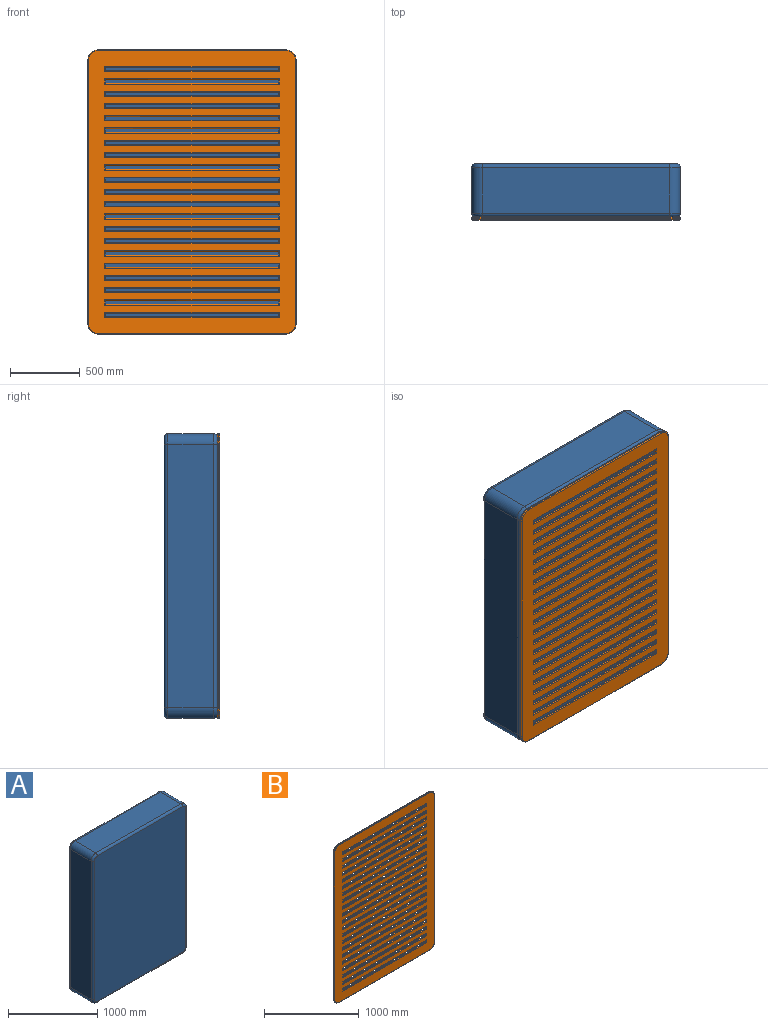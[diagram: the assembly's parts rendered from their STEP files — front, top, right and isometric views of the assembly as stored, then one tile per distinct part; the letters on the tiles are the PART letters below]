
ASSEMBLY  parts=2 mates=1
PART A: 26 faces, bbox 1511.2x381x2057.3 mm
  f0: plane 1892.3x330.2mm, normal (-1,0,0), area 624837.5mm2, adj f1,f7,f14,f22
  f1: cylinder r=76.2mm len=330.2mm, axis (0,1,0), area 39523.2mm2, adj f0,f2,f12,f20
  f2: plane 1346.2x330.2mm, normal (0,0,-1), area 444515.2mm2, adj f1,f3,f10,f18
  f3: cylinder r=76.2mm len=330.2mm, axis (0,1,0), area 39523.2mm2, adj f2,f4,f11,f19
  f4: plane 1892.3x330.2mm, normal (1,0,0), area 624837.5mm2, adj f3,f5,f13,f21
  f5: cylinder r=76.2mm len=330.2mm, axis (0,1,0), area 39523.2mm2, adj f4,f6,f15,f23
  f6: plane 1346.2x330.2mm, normal (0,0,1), area 444515.2mm2, adj f5,f7,f17,f25
  f7: cylinder r=76.2mm len=330.2mm, axis (0,1,0), area 39523.2mm2, adj f0,f6,f16,f24
  f8: plane 1993.9x1447.8mm, normal (0,-1,0), area 2884553.2mm2, adj f18,f19,f20,f21,f22,f23,f24,f25
  f9: plane 1993.9x1447.8mm, normal (0,1,0), area 2884553.2mm2, adj f10,f11,f12,f13,f14,f15,f16,f17
  f10: cylinder r=25.4mm len=1346.2mm, axis (1,0,0), area 53711mm2, adj f2,f9,f11,f12
  f11: torus R=50.8mm, axis (0,-1,0), area 4197.2mm2, adj f3,f9,f10,f13
  f12: torus R=50.8mm, axis (0,-1,0), area 4197.2mm2, adj f1,f9,f10,f14
  f13: cylinder r=25.4mm len=1892.3mm, axis (0,0,1), area 75499.4mm2, adj f4,f9,f11,f15
  f14: cylinder r=25.4mm len=1892.3mm, axis (0,0,-1), area 75499.4mm2, adj f0,f9,f12,f16
  f15: torus R=50.8mm, axis (0,-1,0), area 4197.2mm2, adj f5,f9,f13,f17
  f16: torus R=50.8mm, axis (0,-1,0), area 4197.2mm2, adj f7,f9,f14,f17
  f17: cylinder r=25.4mm len=1346.2mm, axis (-1,0,0), area 53711mm2, adj f6,f9,f15,f16
  f18: cylinder r=25.4mm len=1346.2mm, axis (-1,0,0), area 53711mm2, adj f2,f8,f19,f20
  f19: torus R=50.8mm, axis (0,-1,0), area 4197.2mm2, adj f3,f8,f18,f21
  f20: torus R=50.8mm, axis (0,-1,0), area 4197.2mm2, adj f1,f8,f18,f22
  f21: cylinder r=25.4mm len=1892.3mm, axis (0,0,-1), area 75499.4mm2, adj f4,f8,f19,f23
  f22: cylinder r=25.4mm len=1892.3mm, axis (0,0,1), area 75499.4mm2, adj f0,f8,f20,f24
  f23: torus R=50.8mm, axis (0,-1,0), area 4197.2mm2, adj f5,f8,f21,f25
  f24: torus R=50.8mm, axis (0,-1,0), area 4197.2mm2, adj f7,f8,f22,f25
  f25: cylinder r=25.4mm len=1346.2mm, axis (1,0,0), area 53711mm2, adj f6,f8,f23,f24
PART B: 278 faces, bbox 1511.2x19.1x2057.3 mm
  f0: plane 2032x1485.9mm, normal (0,-1,0), area 2009194.9mm2, adj f178,f179,f180,f181,f182,f183,f184,f185
  f1: plane 2032x1485.9mm, normal (0,1,0), area 2009194.9mm2, adj f94,f95,f96,f97,f98,f99,f100,f101
  f2: plane 1892.3x6.35mm, normal (-1,0,0), area 12016.1mm2, adj f3,f9,f266,f274
  f3: cylinder r=76.2mm len=76.2mm, axis (0,1,0), area 760.1mm2, adj f2,f4,f264,f272
  f4: plane 1346.2x6.35mm, normal (0,0,-1), area 8548.4mm2, adj f3,f5,f262,f270
  f5: cylinder r=76.2mm len=76.2mm, axis (0,1,0), area 760.1mm2, adj f4,f6,f263,f271
  f6: plane 1892.3x6.35mm, normal (1,0,0), area 12016.1mm2, adj f5,f7,f265,f273
  f7: cylinder r=76.2mm len=76.2mm, axis (0,1,0), area 760.1mm2, adj f6,f8,f267,f275
  f8: plane 1346.2x6.35mm, normal (0,0,1), area 8548.4mm2, adj f7,f9,f269,f277
  f9: cylinder r=76.2mm len=76.2mm, axis (0,1,0), area 760.1mm2, adj f2,f8,f268,f276
  f10: plane 1244.6x6.35mm, normal (0,0,-1), area 7903.2mm2, adj f11,f13,f177,f179
  f11: plane 25.4x6.35mm, normal (1,0,0), area 161.3mm2, adj f10,f12,f175,f181
  f12: plane 1244.6x6.35mm, normal (0,0,1), area 7903.2mm2, adj f11,f13,f174,f180
  f13: plane 25.4x6.35mm, normal (-1,0,0), area 161.3mm2, adj f10,f12,f176,f178
  f14: plane 1244.6x6.35mm, normal (0,0,-1), area 7903.2mm2, adj f15,f17,f173,f183
  f15: plane 25.4x6.35mm, normal (1,0,0), area 161.3mm2, adj f14,f16,f171,f185
  f16: plane 1244.6x6.35mm, normal (0,0,1), area 7903.2mm2, adj f15,f17,f170,f184
  f17: plane 25.4x6.35mm, normal (-1,0,0), area 161.3mm2, adj f14,f16,f172,f182
  f18: plane 1244.6x6.35mm, normal (0,0,-1), area 7903.2mm2, adj f19,f21,f169,f187
  f19: plane 25.4x6.35mm, normal (1,0,0), area 161.3mm2, adj f18,f20,f167,f189
  f20: plane 1244.6x6.35mm, normal (0,0,1), area 7903.2mm2, adj f19,f21,f166,f188
  f21: plane 25.4x6.35mm, normal (-1,0,0), area 161.3mm2, adj f18,f20,f168,f186
  f22: plane 1244.6x6.35mm, normal (0,0,-1), area 7903.2mm2, adj f23,f25,f165,f191
  f23: plane 25.4x6.35mm, normal (1,0,0), area 161.3mm2, adj f22,f24,f163,f193
  f24: plane 1244.6x6.35mm, normal (0,0,1), area 7903.2mm2, adj f23,f25,f162,f192
  f25: plane 25.4x6.35mm, normal (-1,0,0), area 161.3mm2, adj f22,f24,f164,f190
  f26: plane 1244.6x6.35mm, normal (0,0,-1), area 7903.2mm2, adj f27,f29,f161,f195
  f27: plane 25.4x6.35mm, normal (1,0,0), area 161.3mm2, adj f26,f28,f159,f197
  f28: plane 1244.6x6.35mm, normal (0,0,1), area 7903.2mm2, adj f27,f29,f158,f196
  f29: plane 25.4x6.35mm, normal (-1,0,0), area 161.3mm2, adj f26,f28,f160,f194
  f30: plane 1244.6x6.35mm, normal (0,0,-1), area 7903.2mm2, adj f31,f33,f157,f199
  f31: plane 25.4x6.35mm, normal (1,0,0), area 161.3mm2, adj f30,f32,f155,f201
  f32: plane 1244.6x6.35mm, normal (0,0,1), area 7903.2mm2, adj f31,f33,f154,f200
  f33: plane 25.4x6.35mm, normal (-1,0,0), area 161.3mm2, adj f30,f32,f156,f198
  f34: plane 1244.6x6.35mm, normal (0,0,-1), area 7903.2mm2, adj f35,f37,f153,f203
  f35: plane 25.4x6.35mm, normal (1,0,0), area 161.3mm2, adj f34,f36,f151,f205
  f36: plane 1244.6x6.35mm, normal (0,0,1), area 7903.2mm2, adj f35,f37,f150,f204
  f37: plane 25.4x6.35mm, normal (-1,0,0), area 161.3mm2, adj f34,f36,f152,f202
  f38: plane 1244.6x6.35mm, normal (0,0,-1), area 7903.2mm2, adj f39,f41,f149,f207
  f39: plane 25.4x6.35mm, normal (1,0,0), area 161.3mm2, adj f38,f40,f147,f209
  f40: plane 1244.6x6.35mm, normal (0,0,1), area 7903.2mm2, adj f39,f41,f146,f208
  f41: plane 25.4x6.35mm, normal (-1,0,0), area 161.3mm2, adj f38,f40,f148,f206
  f42: plane 1244.6x6.35mm, normal (0,0,-1), area 7903.2mm2, adj f43,f45,f145,f211
  f43: plane 25.4x6.35mm, normal (1,0,0), area 161.3mm2, adj f42,f44,f143,f213
  f44: plane 1244.6x6.35mm, normal (0,0,1), area 7903.2mm2, adj f43,f45,f142,f212
  f45: plane 25.4x6.35mm, normal (-1,0,0), area 161.3mm2, adj f42,f44,f144,f210
  f46: plane 1244.6x6.35mm, normal (0,0,-1), area 7903.2mm2, adj f47,f49,f141,f215
  f47: plane 25.4x6.35mm, normal (1,0,0), area 161.3mm2, adj f46,f48,f139,f217
  f48: plane 1244.6x6.35mm, normal (0,0,1), area 7903.2mm2, adj f47,f49,f138,f216
  f49: plane 25.4x6.35mm, normal (-1,0,0), area 161.3mm2, adj f46,f48,f140,f214
  f50: plane 1244.6x6.35mm, normal (0,0,-1), area 7903.2mm2, adj f51,f53,f137,f219
  f51: plane 25.4x6.35mm, normal (1,0,0), area 161.3mm2, adj f50,f52,f135,f221
  f52: plane 1244.6x6.35mm, normal (0,0,1), area 7903.2mm2, adj f51,f53,f134,f220
  f53: plane 25.4x6.35mm, normal (-1,0,0), area 161.3mm2, adj f50,f52,f136,f218
  f54: plane 1244.6x6.35mm, normal (0,0,-1), area 7903.2mm2, adj f55,f57,f133,f223
  f55: plane 25.4x6.35mm, normal (1,0,0), area 161.3mm2, adj f54,f56,f131,f225
  f56: plane 1244.6x6.35mm, normal (0,0,1), area 7903.2mm2, adj f55,f57,f130,f224
  f57: plane 25.4x6.35mm, normal (-1,0,0), area 161.3mm2, adj f54,f56,f132,f222
  f58: plane 1244.6x6.35mm, normal (0,0,-1), area 7903.2mm2, adj f59,f61,f129,f227
  f59: plane 25.4x6.35mm, normal (1,0,0), area 161.3mm2, adj f58,f60,f127,f229
  f60: plane 1244.6x6.35mm, normal (0,0,1), area 7903.2mm2, adj f59,f61,f126,f228
  f61: plane 25.4x6.35mm, normal (-1,0,0), area 161.3mm2, adj f58,f60,f128,f226
  f62: plane 1244.6x6.35mm, normal (0,0,-1), area 7903.2mm2, adj f63,f65,f125,f231
  f63: plane 25.4x6.35mm, normal (1,0,0), area 161.3mm2, adj f62,f64,f123,f233
  f64: plane 1244.6x6.35mm, normal (0,0,1), area 7903.2mm2, adj f63,f65,f122,f232
  f65: plane 25.4x6.35mm, normal (-1,0,0), area 161.3mm2, adj f62,f64,f124,f230
  f66: plane 1244.6x6.35mm, normal (0,0,-1), area 7903.2mm2, adj f67,f69,f121,f235
  f67: plane 25.4x6.35mm, normal (1,0,0), area 161.3mm2, adj f66,f68,f119,f237
  f68: plane 1244.6x6.35mm, normal (0,0,1), area 7903.2mm2, adj f67,f69,f118,f236
  f69: plane 25.4x6.35mm, normal (-1,0,0), area 161.3mm2, adj f66,f68,f120,f234
  f70: plane 1244.6x6.35mm, normal (0,0,-1), area 7903.2mm2, adj f71,f73,f117,f239
  f71: plane 25.4x6.35mm, normal (1,0,0), area 161.3mm2, adj f70,f72,f115,f241
  f72: plane 1244.6x6.35mm, normal (0,0,1), area 7903.2mm2, adj f71,f73,f114,f240
  f73: plane 25.4x6.35mm, normal (-1,0,0), area 161.3mm2, adj f70,f72,f116,f238
  f74: plane 1244.6x6.35mm, normal (0,0,-1), area 7903.2mm2, adj f75,f77,f113,f243
  f75: plane 25.4x6.35mm, normal (1,0,0), area 161.3mm2, adj f74,f76,f111,f245
  f76: plane 1244.6x6.35mm, normal (0,0,1), area 7903.2mm2, adj f75,f77,f110,f244
  f77: plane 25.4x6.35mm, normal (-1,0,0), area 161.3mm2, adj f74,f76,f112,f242
  f78: plane 1244.6x6.35mm, normal (0,0,-1), area 7903.2mm2, adj f79,f81,f109,f247
  f79: plane 25.4x6.35mm, normal (1,0,0), area 161.3mm2, adj f78,f80,f107,f249
  f80: plane 1244.6x6.35mm, normal (0,0,1), area 7903.2mm2, adj f79,f81,f106,f248
  f81: plane 25.4x6.35mm, normal (-1,0,0), area 161.3mm2, adj f78,f80,f108,f246
  f82: plane 1244.6x6.35mm, normal (0,0,-1), area 7903.2mm2, adj f83,f85,f105,f251
  f83: plane 25.4x6.35mm, normal (1,0,0), area 161.3mm2, adj f82,f84,f103,f253
  f84: plane 1244.6x6.35mm, normal (0,0,1), area 7903.2mm2, adj f83,f85,f102,f252
  f85: plane 25.4x6.35mm, normal (-1,0,0), area 161.3mm2, adj f82,f84,f104,f250
  f86: plane 1244.6x6.35mm, normal (0,0,-1), area 7903.2mm2, adj f87,f89,f101,f254
  f87: plane 25.4x6.35mm, normal (1,0,0), area 161.3mm2, adj f86,f88,f99,f255
  f88: plane 1244.6x6.35mm, normal (0,0,1), area 7903.2mm2, adj f87,f89,f98,f257
  f89: plane 25.4x6.35mm, normal (-1,0,0), area 161.3mm2, adj f86,f88,f100,f256
  f90: plane 1244.6x6.35mm, normal (0,0,-1), area 7903.2mm2, adj f91,f93,f97,f259
  f91: plane 25.4x6.35mm, normal (1,0,0), area 161.3mm2, adj f90,f92,f95,f261
  f92: plane 1244.6x6.35mm, normal (0,0,1), area 7903.2mm2, adj f91,f93,f94,f260
  f93: plane 25.4x6.35mm, normal (-1,0,0), area 161.3mm2, adj f90,f92,f96,f258
  f94: cylinder r=6.35mm len=1257.3mm, axis (1,0,0), area 12460.4mm2, adj f1,f92,f95,f96
  f95: cylinder r=6.35mm len=38.1mm, axis (0,0,-1), area 299.4mm2, adj f1,f91,f94,f97
  f96: cylinder r=6.35mm len=38.1mm, axis (0,0,1), area 299.4mm2, adj f1,f93,f94,f97
  f97: cylinder r=6.35mm len=1257.3mm, axis (-1,0,0), area 12460.4mm2, adj f1,f90,f95,f96
  f98: cylinder r=6.35mm len=1257.3mm, axis (1,0,0), area 12460.4mm2, adj f1,f88,f99,f100
  f99: cylinder r=6.35mm len=38.1mm, axis (0,0,-1), area 299.4mm2, adj f1,f87,f98,f101
  f100: cylinder r=6.35mm len=38.1mm, axis (0,0,1), area 299.4mm2, adj f1,f89,f98,f101
  f101: cylinder r=6.35mm len=1257.3mm, axis (-1,0,0), area 12460.4mm2, adj f1,f86,f99,f100
  f102: cylinder r=6.35mm len=1257.3mm, axis (1,0,0), area 12460.4mm2, adj f1,f84,f103,f104
  f103: cylinder r=6.35mm len=38.1mm, axis (0,0,-1), area 299.4mm2, adj f1,f83,f102,f105
  f104: cylinder r=6.35mm len=38.1mm, axis (0,0,1), area 299.4mm2, adj f1,f85,f102,f105
  f105: cylinder r=6.35mm len=1257.3mm, axis (-1,0,0), area 12460.4mm2, adj f1,f82,f103,f104
  f106: cylinder r=6.35mm len=1257.3mm, axis (1,0,0), area 12460.4mm2, adj f1,f80,f107,f108
  f107: cylinder r=6.35mm len=38.1mm, axis (0,0,-1), area 299.4mm2, adj f1,f79,f106,f109
  f108: cylinder r=6.35mm len=38.1mm, axis (0,0,1), area 299.4mm2, adj f1,f81,f106,f109
  f109: cylinder r=6.35mm len=1257.3mm, axis (-1,0,0), area 12460.4mm2, adj f1,f78,f107,f108
  f110: cylinder r=6.35mm len=1257.3mm, axis (1,0,0), area 12460.4mm2, adj f1,f76,f111,f112
  f111: cylinder r=6.35mm len=38.1mm, axis (0,0,-1), area 299.4mm2, adj f1,f75,f110,f113
  f112: cylinder r=6.35mm len=38.1mm, axis (0,0,1), area 299.4mm2, adj f1,f77,f110,f113
  f113: cylinder r=6.35mm len=1257.3mm, axis (-1,0,0), area 12460.4mm2, adj f1,f74,f111,f112
  f114: cylinder r=6.35mm len=1257.3mm, axis (1,0,0), area 12460.4mm2, adj f1,f72,f115,f116
  f115: cylinder r=6.35mm len=38.1mm, axis (0,0,-1), area 299.4mm2, adj f1,f71,f114,f117
  f116: cylinder r=6.35mm len=38.1mm, axis (0,0,1), area 299.4mm2, adj f1,f73,f114,f117
  f117: cylinder r=6.35mm len=1257.3mm, axis (-1,0,0), area 12460.4mm2, adj f1,f70,f115,f116
  f118: cylinder r=6.35mm len=1257.3mm, axis (1,0,0), area 12460.4mm2, adj f1,f68,f119,f120
  f119: cylinder r=6.35mm len=38.1mm, axis (0,0,-1), area 299.4mm2, adj f1,f67,f118,f121
  f120: cylinder r=6.35mm len=38.1mm, axis (0,0,1), area 299.4mm2, adj f1,f69,f118,f121
  f121: cylinder r=6.35mm len=1257.3mm, axis (-1,0,0), area 12460.4mm2, adj f1,f66,f119,f120
  f122: cylinder r=6.35mm len=1257.3mm, axis (1,0,0), area 12460.4mm2, adj f1,f64,f123,f124
  f123: cylinder r=6.35mm len=38.1mm, axis (0,0,-1), area 299.4mm2, adj f1,f63,f122,f125
  f124: cylinder r=6.35mm len=38.1mm, axis (0,0,1), area 299.4mm2, adj f1,f65,f122,f125
  f125: cylinder r=6.35mm len=1257.3mm, axis (-1,0,0), area 12460.4mm2, adj f1,f62,f123,f124
  f126: cylinder r=6.35mm len=1257.3mm, axis (1,0,0), area 12460.4mm2, adj f1,f60,f127,f128
  f127: cylinder r=6.35mm len=38.1mm, axis (0,0,-1), area 299.4mm2, adj f1,f59,f126,f129
  f128: cylinder r=6.35mm len=38.1mm, axis (0,0,1), area 299.4mm2, adj f1,f61,f126,f129
  f129: cylinder r=6.35mm len=1257.3mm, axis (-1,0,0), area 12460.4mm2, adj f1,f58,f127,f128
  f130: cylinder r=6.35mm len=1257.3mm, axis (1,0,0), area 12460.4mm2, adj f1,f56,f131,f132
  f131: cylinder r=6.35mm len=38.1mm, axis (0,0,-1), area 299.4mm2, adj f1,f55,f130,f133
  f132: cylinder r=6.35mm len=38.1mm, axis (0,0,1), area 299.4mm2, adj f1,f57,f130,f133
  f133: cylinder r=6.35mm len=1257.3mm, axis (-1,0,0), area 12460.4mm2, adj f1,f54,f131,f132
  f134: cylinder r=6.35mm len=1257.3mm, axis (1,0,0), area 12460.4mm2, adj f1,f52,f135,f136
  f135: cylinder r=6.35mm len=38.1mm, axis (0,0,-1), area 299.4mm2, adj f1,f51,f134,f137
  f136: cylinder r=6.35mm len=38.1mm, axis (0,0,1), area 299.4mm2, adj f1,f53,f134,f137
  f137: cylinder r=6.35mm len=1257.3mm, axis (-1,0,0), area 12460.4mm2, adj f1,f50,f135,f136
  f138: cylinder r=6.35mm len=1257.3mm, axis (1,0,0), area 12460.4mm2, adj f1,f48,f139,f140
  f139: cylinder r=6.35mm len=38.1mm, axis (0,0,-1), area 299.4mm2, adj f1,f47,f138,f141
  f140: cylinder r=6.35mm len=38.1mm, axis (0,0,1), area 299.4mm2, adj f1,f49,f138,f141
  f141: cylinder r=6.35mm len=1257.3mm, axis (-1,0,0), area 12460.4mm2, adj f1,f46,f139,f140
  f142: cylinder r=6.35mm len=1257.3mm, axis (1,0,0), area 12460.4mm2, adj f1,f44,f143,f144
  f143: cylinder r=6.35mm len=38.1mm, axis (0,0,-1), area 299.4mm2, adj f1,f43,f142,f145
  f144: cylinder r=6.35mm len=38.1mm, axis (0,0,1), area 299.4mm2, adj f1,f45,f142,f145
  f145: cylinder r=6.35mm len=1257.3mm, axis (-1,0,0), area 12460.4mm2, adj f1,f42,f143,f144
  f146: cylinder r=6.35mm len=1257.3mm, axis (1,0,0), area 12460.4mm2, adj f1,f40,f147,f148
  f147: cylinder r=6.35mm len=38.1mm, axis (0,0,-1), area 299.4mm2, adj f1,f39,f146,f149
  f148: cylinder r=6.35mm len=38.1mm, axis (0,0,1), area 299.4mm2, adj f1,f41,f146,f149
  f149: cylinder r=6.35mm len=1257.3mm, axis (-1,0,0), area 12460.4mm2, adj f1,f38,f147,f148
  f150: cylinder r=6.35mm len=1257.3mm, axis (1,0,0), area 12460.4mm2, adj f1,f36,f151,f152
  f151: cylinder r=6.35mm len=38.1mm, axis (0,0,-1), area 299.4mm2, adj f1,f35,f150,f153
  f152: cylinder r=6.35mm len=38.1mm, axis (0,0,1), area 299.4mm2, adj f1,f37,f150,f153
  f153: cylinder r=6.35mm len=1257.3mm, axis (-1,0,0), area 12460.4mm2, adj f1,f34,f151,f152
  f154: cylinder r=6.35mm len=1257.3mm, axis (1,0,0), area 12460.4mm2, adj f1,f32,f155,f156
  f155: cylinder r=6.35mm len=38.1mm, axis (0,0,-1), area 299.4mm2, adj f1,f31,f154,f157
  f156: cylinder r=6.35mm len=38.1mm, axis (0,0,1), area 299.4mm2, adj f1,f33,f154,f157
  f157: cylinder r=6.35mm len=1257.3mm, axis (-1,0,0), area 12460.4mm2, adj f1,f30,f155,f156
  f158: cylinder r=6.35mm len=1257.3mm, axis (1,0,0), area 12460.4mm2, adj f1,f28,f159,f160
  f159: cylinder r=6.35mm len=38.1mm, axis (0,0,-1), area 299.4mm2, adj f1,f27,f158,f161
  f160: cylinder r=6.35mm len=38.1mm, axis (0,0,1), area 299.4mm2, adj f1,f29,f158,f161
  f161: cylinder r=6.35mm len=1257.3mm, axis (-1,0,0), area 12460.4mm2, adj f1,f26,f159,f160
  f162: cylinder r=6.35mm len=1257.3mm, axis (1,0,0), area 12460.4mm2, adj f1,f24,f163,f164
  f163: cylinder r=6.35mm len=38.1mm, axis (0,0,-1), area 299.4mm2, adj f1,f23,f162,f165
  f164: cylinder r=6.35mm len=38.1mm, axis (0,0,1), area 299.4mm2, adj f1,f25,f162,f165
  f165: cylinder r=6.35mm len=1257.3mm, axis (-1,0,0), area 12460.4mm2, adj f1,f22,f163,f164
  f166: cylinder r=6.35mm len=1257.3mm, axis (1,0,0), area 12460.4mm2, adj f1,f20,f167,f168
  f167: cylinder r=6.35mm len=38.1mm, axis (0,0,-1), area 299.4mm2, adj f1,f19,f166,f169
  f168: cylinder r=6.35mm len=38.1mm, axis (0,0,1), area 299.4mm2, adj f1,f21,f166,f169
  f169: cylinder r=6.35mm len=1257.3mm, axis (-1,0,0), area 12460.4mm2, adj f1,f18,f167,f168
  f170: cylinder r=6.35mm len=1257.3mm, axis (1,0,0), area 12460.4mm2, adj f1,f16,f171,f172
  f171: cylinder r=6.35mm len=38.1mm, axis (0,0,-1), area 299.4mm2, adj f1,f15,f170,f173
  f172: cylinder r=6.35mm len=38.1mm, axis (0,0,1), area 299.4mm2, adj f1,f17,f170,f173
  f173: cylinder r=6.35mm len=1257.3mm, axis (-1,0,0), area 12460.4mm2, adj f1,f14,f171,f172
  f174: cylinder r=6.35mm len=1257.3mm, axis (1,0,0), area 12460.4mm2, adj f1,f12,f175,f176
  f175: cylinder r=6.35mm len=38.1mm, axis (0,0,-1), area 299.4mm2, adj f1,f11,f174,f177
  f176: cylinder r=6.35mm len=38.1mm, axis (0,0,1), area 299.4mm2, adj f1,f13,f174,f177
  f177: cylinder r=6.35mm len=1257.3mm, axis (-1,0,0), area 12460.4mm2, adj f1,f10,f175,f176
  f178: cylinder r=6.35mm len=38.1mm, axis (0,0,-1), area 299.4mm2, adj f0,f13,f179,f180
  f179: cylinder r=6.35mm len=1257.3mm, axis (1,0,0), area 12460.4mm2, adj f0,f10,f178,f181
  f180: cylinder r=6.35mm len=1257.3mm, axis (-1,0,0), area 12460.4mm2, adj f0,f12,f178,f181
  f181: cylinder r=6.35mm len=38.1mm, axis (0,0,1), area 299.4mm2, adj f0,f11,f179,f180
  f182: cylinder r=6.35mm len=38.1mm, axis (0,0,-1), area 299.4mm2, adj f0,f17,f183,f184
  f183: cylinder r=6.35mm len=1257.3mm, axis (1,0,0), area 12460.4mm2, adj f0,f14,f182,f185
  f184: cylinder r=6.35mm len=1257.3mm, axis (-1,0,0), area 12460.4mm2, adj f0,f16,f182,f185
  f185: cylinder r=6.35mm len=38.1mm, axis (0,0,1), area 299.4mm2, adj f0,f15,f183,f184
  f186: cylinder r=6.35mm len=38.1mm, axis (0,0,-1), area 299.4mm2, adj f0,f21,f187,f188
  f187: cylinder r=6.35mm len=1257.3mm, axis (1,0,0), area 12460.4mm2, adj f0,f18,f186,f189
  f188: cylinder r=6.35mm len=1257.3mm, axis (-1,0,0), area 12460.4mm2, adj f0,f20,f186,f189
  f189: cylinder r=6.35mm len=38.1mm, axis (0,0,1), area 299.4mm2, adj f0,f19,f187,f188
  f190: cylinder r=6.35mm len=38.1mm, axis (0,0,-1), area 299.4mm2, adj f0,f25,f191,f192
  f191: cylinder r=6.35mm len=1257.3mm, axis (1,0,0), area 12460.4mm2, adj f0,f22,f190,f193
  f192: cylinder r=6.35mm len=1257.3mm, axis (-1,0,0), area 12460.4mm2, adj f0,f24,f190,f193
  f193: cylinder r=6.35mm len=38.1mm, axis (0,0,1), area 299.4mm2, adj f0,f23,f191,f192
  f194: cylinder r=6.35mm len=38.1mm, axis (0,0,-1), area 299.4mm2, adj f0,f29,f195,f196
  f195: cylinder r=6.35mm len=1257.3mm, axis (1,0,0), area 12460.4mm2, adj f0,f26,f194,f197
  f196: cylinder r=6.35mm len=1257.3mm, axis (-1,0,0), area 12460.4mm2, adj f0,f28,f194,f197
  f197: cylinder r=6.35mm len=38.1mm, axis (0,0,1), area 299.4mm2, adj f0,f27,f195,f196
  f198: cylinder r=6.35mm len=38.1mm, axis (0,0,-1), area 299.4mm2, adj f0,f33,f199,f200
  f199: cylinder r=6.35mm len=1257.3mm, axis (1,0,0), area 12460.4mm2, adj f0,f30,f198,f201
  f200: cylinder r=6.35mm len=1257.3mm, axis (-1,0,0), area 12460.4mm2, adj f0,f32,f198,f201
  f201: cylinder r=6.35mm len=38.1mm, axis (0,0,1), area 299.4mm2, adj f0,f31,f199,f200
  f202: cylinder r=6.35mm len=38.1mm, axis (0,0,-1), area 299.4mm2, adj f0,f37,f203,f204
  f203: cylinder r=6.35mm len=1257.3mm, axis (1,0,0), area 12460.4mm2, adj f0,f34,f202,f205
  f204: cylinder r=6.35mm len=1257.3mm, axis (-1,0,0), area 12460.4mm2, adj f0,f36,f202,f205
  f205: cylinder r=6.35mm len=38.1mm, axis (0,0,1), area 299.4mm2, adj f0,f35,f203,f204
  f206: cylinder r=6.35mm len=38.1mm, axis (0,0,-1), area 299.4mm2, adj f0,f41,f207,f208
  f207: cylinder r=6.35mm len=1257.3mm, axis (1,0,0), area 12460.4mm2, adj f0,f38,f206,f209
  f208: cylinder r=6.35mm len=1257.3mm, axis (-1,0,0), area 12460.4mm2, adj f0,f40,f206,f209
  f209: cylinder r=6.35mm len=38.1mm, axis (0,0,1), area 299.4mm2, adj f0,f39,f207,f208
  f210: cylinder r=6.35mm len=38.1mm, axis (0,0,-1), area 299.4mm2, adj f0,f45,f211,f212
  f211: cylinder r=6.35mm len=1257.3mm, axis (1,0,0), area 12460.4mm2, adj f0,f42,f210,f213
  f212: cylinder r=6.35mm len=1257.3mm, axis (-1,0,0), area 12460.4mm2, adj f0,f44,f210,f213
  f213: cylinder r=6.35mm len=38.1mm, axis (0,0,1), area 299.4mm2, adj f0,f43,f211,f212
  f214: cylinder r=6.35mm len=38.1mm, axis (0,0,-1), area 299.4mm2, adj f0,f49,f215,f216
  f215: cylinder r=6.35mm len=1257.3mm, axis (1,0,0), area 12460.4mm2, adj f0,f46,f214,f217
  f216: cylinder r=6.35mm len=1257.3mm, axis (-1,0,0), area 12460.4mm2, adj f0,f48,f214,f217
  f217: cylinder r=6.35mm len=38.1mm, axis (0,0,1), area 299.4mm2, adj f0,f47,f215,f216
  f218: cylinder r=6.35mm len=38.1mm, axis (0,0,-1), area 299.4mm2, adj f0,f53,f219,f220
  f219: cylinder r=6.35mm len=1257.3mm, axis (1,0,0), area 12460.4mm2, adj f0,f50,f218,f221
  f220: cylinder r=6.35mm len=1257.3mm, axis (-1,0,0), area 12460.4mm2, adj f0,f52,f218,f221
  f221: cylinder r=6.35mm len=38.1mm, axis (0,0,1), area 299.4mm2, adj f0,f51,f219,f220
  f222: cylinder r=6.35mm len=38.1mm, axis (0,0,-1), area 299.4mm2, adj f0,f57,f223,f224
  f223: cylinder r=6.35mm len=1257.3mm, axis (1,0,0), area 12460.4mm2, adj f0,f54,f222,f225
  f224: cylinder r=6.35mm len=1257.3mm, axis (-1,0,0), area 12460.4mm2, adj f0,f56,f222,f225
  f225: cylinder r=6.35mm len=38.1mm, axis (0,0,1), area 299.4mm2, adj f0,f55,f223,f224
  f226: cylinder r=6.35mm len=38.1mm, axis (0,0,-1), area 299.4mm2, adj f0,f61,f227,f228
  f227: cylinder r=6.35mm len=1257.3mm, axis (1,0,0), area 12460.4mm2, adj f0,f58,f226,f229
  f228: cylinder r=6.35mm len=1257.3mm, axis (-1,0,0), area 12460.4mm2, adj f0,f60,f226,f229
  f229: cylinder r=6.35mm len=38.1mm, axis (0,0,1), area 299.4mm2, adj f0,f59,f227,f228
  f230: cylinder r=6.35mm len=38.1mm, axis (0,0,-1), area 299.4mm2, adj f0,f65,f231,f232
  f231: cylinder r=6.35mm len=1257.3mm, axis (1,0,0), area 12460.4mm2, adj f0,f62,f230,f233
  f232: cylinder r=6.35mm len=1257.3mm, axis (-1,0,0), area 12460.4mm2, adj f0,f64,f230,f233
  f233: cylinder r=6.35mm len=38.1mm, axis (0,0,1), area 299.4mm2, adj f0,f63,f231,f232
  f234: cylinder r=6.35mm len=38.1mm, axis (0,0,-1), area 299.4mm2, adj f0,f69,f235,f236
  f235: cylinder r=6.35mm len=1257.3mm, axis (1,0,0), area 12460.4mm2, adj f0,f66,f234,f237
  f236: cylinder r=6.35mm len=1257.3mm, axis (-1,0,0), area 12460.4mm2, adj f0,f68,f234,f237
  f237: cylinder r=6.35mm len=38.1mm, axis (0,0,1), area 299.4mm2, adj f0,f67,f235,f236
  f238: cylinder r=6.35mm len=38.1mm, axis (0,0,-1), area 299.4mm2, adj f0,f73,f239,f240
  f239: cylinder r=6.35mm len=1257.3mm, axis (1,0,0), area 12460.4mm2, adj f0,f70,f238,f241
  f240: cylinder r=6.35mm len=1257.3mm, axis (-1,0,0), area 12460.4mm2, adj f0,f72,f238,f241
  f241: cylinder r=6.35mm len=38.1mm, axis (0,0,1), area 299.4mm2, adj f0,f71,f239,f240
  f242: cylinder r=6.35mm len=38.1mm, axis (0,0,-1), area 299.4mm2, adj f0,f77,f243,f244
  f243: cylinder r=6.35mm len=1257.3mm, axis (1,0,0), area 12460.4mm2, adj f0,f74,f242,f245
  f244: cylinder r=6.35mm len=1257.3mm, axis (-1,0,0), area 12460.4mm2, adj f0,f76,f242,f245
  f245: cylinder r=6.35mm len=38.1mm, axis (0,0,1), area 299.4mm2, adj f0,f75,f243,f244
  f246: cylinder r=6.35mm len=38.1mm, axis (0,0,-1), area 299.4mm2, adj f0,f81,f247,f248
  f247: cylinder r=6.35mm len=1257.3mm, axis (1,0,0), area 12460.4mm2, adj f0,f78,f246,f249
  f248: cylinder r=6.35mm len=1257.3mm, axis (-1,0,0), area 12460.4mm2, adj f0,f80,f246,f249
  f249: cylinder r=6.35mm len=38.1mm, axis (0,0,1), area 299.4mm2, adj f0,f79,f247,f248
  f250: cylinder r=6.35mm len=38.1mm, axis (0,0,-1), area 299.4mm2, adj f0,f85,f251,f252
  f251: cylinder r=6.35mm len=1257.3mm, axis (1,0,0), area 12460.4mm2, adj f0,f82,f250,f253
  f252: cylinder r=6.35mm len=1257.3mm, axis (-1,0,0), area 12460.4mm2, adj f0,f84,f250,f253
  f253: cylinder r=6.35mm len=38.1mm, axis (0,0,1), area 299.4mm2, adj f0,f83,f251,f252
  f254: cylinder r=6.35mm len=1257.3mm, axis (1,0,0), area 12460.4mm2, adj f0,f86,f255,f256
  f255: cylinder r=6.35mm len=38.1mm, axis (0,0,1), area 299.4mm2, adj f0,f87,f254,f257
  f256: cylinder r=6.35mm len=38.1mm, axis (0,0,-1), area 299.4mm2, adj f0,f89,f254,f257
  f257: cylinder r=6.35mm len=1257.3mm, axis (-1,0,0), area 12460.4mm2, adj f0,f88,f255,f256
  f258: cylinder r=6.35mm len=38.1mm, axis (0,0,-1), area 299.4mm2, adj f0,f93,f259,f260
  f259: cylinder r=6.35mm len=1257.3mm, axis (1,0,0), area 12460.4mm2, adj f0,f90,f258,f261
  f260: cylinder r=6.35mm len=1257.3mm, axis (-1,0,0), area 12460.4mm2, adj f0,f92,f258,f261
  f261: cylinder r=6.35mm len=38.1mm, axis (0,0,1), area 299.4mm2, adj f0,f91,f259,f260
  f262: cylinder r=6.35mm len=1346.2mm, axis (1,0,0), area 13427.7mm2, adj f1,f4,f263,f264
  f263: torus R=69.85mm, axis (0,-1,0), area 1157.7mm2, adj f1,f5,f262,f265
  f264: torus R=69.85mm, axis (0,-1,0), area 1157.7mm2, adj f1,f3,f262,f266
  f265: cylinder r=6.35mm len=1892.3mm, axis (0,0,1), area 18874.9mm2, adj f1,f6,f263,f267
  f266: cylinder r=6.35mm len=1892.3mm, axis (0,0,-1), area 18874.9mm2, adj f1,f2,f264,f268
  f267: torus R=69.85mm, axis (0,-1,0), area 1157.7mm2, adj f1,f7,f265,f269
  f268: torus R=69.85mm, axis (0,-1,0), area 1157.7mm2, adj f1,f9,f266,f269
  f269: cylinder r=6.35mm len=1346.2mm, axis (-1,0,0), area 13427.7mm2, adj f1,f8,f267,f268
  f270: cylinder r=6.35mm len=1346.2mm, axis (-1,0,0), area 13427.7mm2, adj f0,f4,f271,f272
  f271: torus R=69.85mm, axis (0,-1,0), area 1157.7mm2, adj f0,f5,f270,f273
  f272: torus R=69.85mm, axis (0,-1,0), area 1157.7mm2, adj f0,f3,f270,f274
  f273: cylinder r=6.35mm len=1892.3mm, axis (0,0,-1), area 18874.9mm2, adj f0,f6,f271,f275
  f274: cylinder r=6.35mm len=1892.3mm, axis (0,0,1), area 18874.9mm2, adj f0,f2,f272,f276
  f275: torus R=69.85mm, axis (0,-1,0), area 1157.7mm2, adj f0,f7,f273,f277
  f276: torus R=69.85mm, axis (0,-1,0), area 1157.7mm2, adj f0,f9,f274,f277
  f277: cylinder r=6.35mm len=1346.2mm, axis (1,0,0), area 13427.7mm2, adj f0,f8,f275,f276
PLACE A t=(-2250.57,1035.53,-103.31)mm
PLACE B rot(axis=(1,0,0),180deg) t=(1444.69,635.48,2744.83)mm
MATE fastened B.f0 <-> A.f8  axis (0,1,0) through (-2962.94,654.53,643.35)mm
